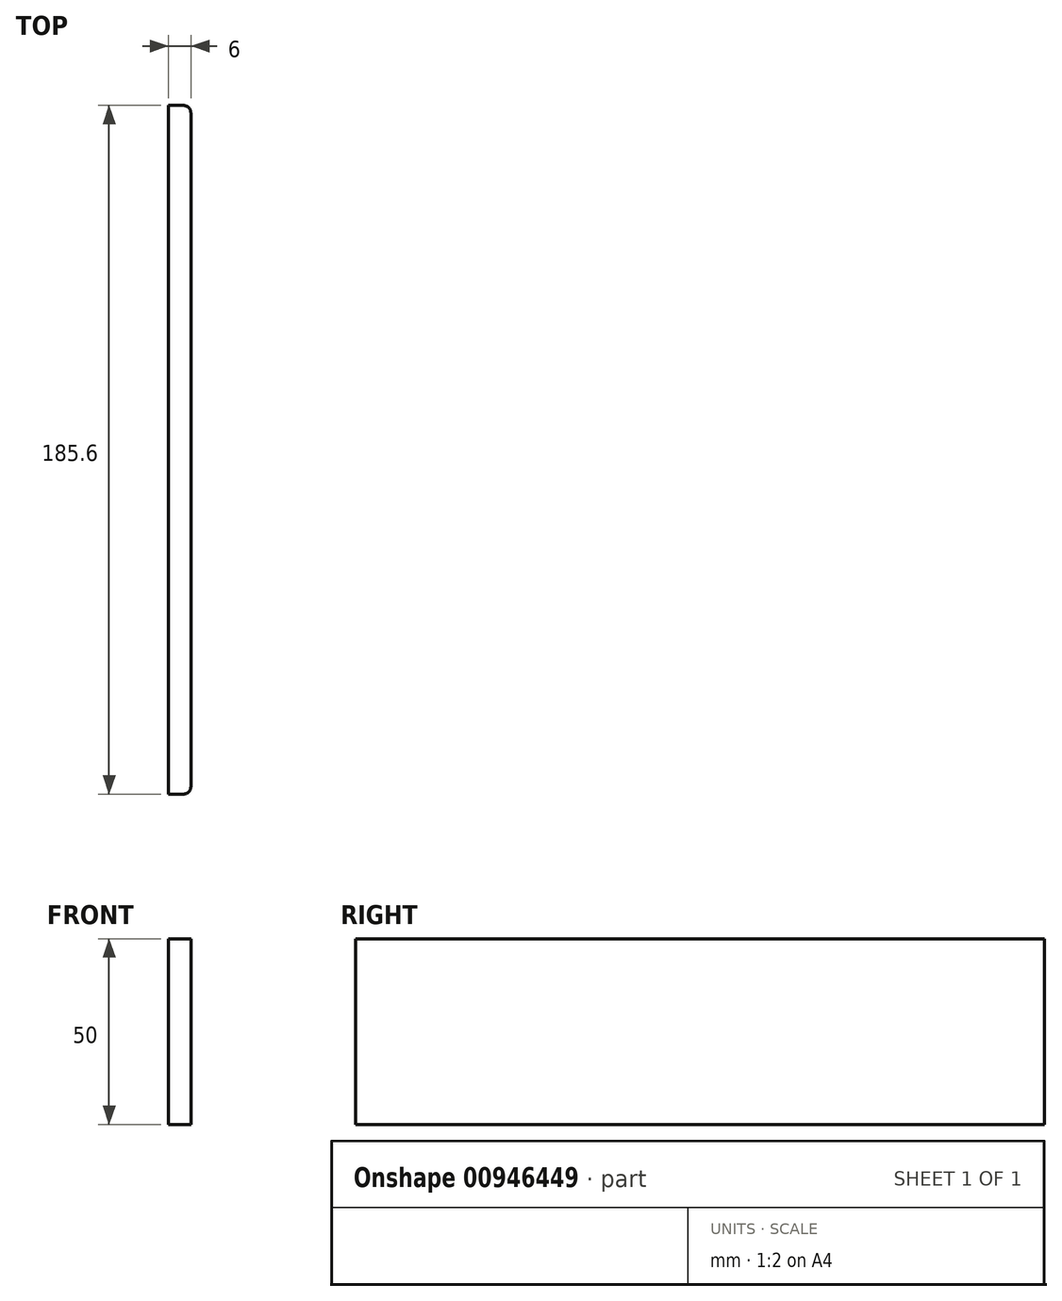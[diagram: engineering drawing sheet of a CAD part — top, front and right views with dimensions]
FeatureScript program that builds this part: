
annotation { "Feature Type Name" : "Feature", "Feature Type Description" : "" }
export const myFeature = defineFeature(function(context is Context, id is Id, definition is map)
    precondition{}
    {
        {
            var Q0;
            Q0=qCreatedBy(makeId("Right.planeOp"),FACE);
            var sketch = newSketch(context, id + "F0", { "sketchPlane" : qUnion([Q0])});
            skLineSegment(sketch, "E0.bottom", {"start": v(92.8, 25) * mm, "end": v(-92.8, 25) * mm});
            skLineSegment(sketch, "E0.top", {"start": v(92.8, -25) * mm, "end": v(-92.8, -25) * mm});
            skLineSegment(sketch, "E0.left", {"start": v(92.8, 25) * mm, "end": v(92.8, -25) * mm});
            skLineSegment(sketch, "E0.right", {"start": v(-92.8, 25) * mm, "end": v(-92.8, -25) * mm});
            skPoint(sketch, "E0.middle", {"position": v(0, 0) * mm});
            skSolve(sketch);
        }
        {
            var Q0;
            Q0=makeQuery(id+"F0.imprint","IMPRINT",FACE,{"disambiguationData":[TD([[makeQuery(id+"F0.imprint","IMPRINT",EDGE,{"derivedFrom":sQuery(id+"F0.wireOp",EDGE,"E0.bottom")}),1.0]])]});
            extrude(context, id + "F1", {"entities" : qUnion([Q0]), "depth" : 6 * mm, "offsetDistance" : 25 * mm});
        }
        {
            var Q0;
            Q0=makeQuery(id+"F1.opExtrude","CAP_EDGE",EDGE,{"disambiguationData":[OSD([sQuery(id+"F0.wireOp",EDGE,"E0.right")])],"isStart":false});
            var Q1;
            Q1=makeQuery(id+"F1.opExtrude","CAP_EDGE",EDGE,{"disambiguationData":[OSD([sQuery(id+"F0.wireOp",EDGE,"E0.left")])],"isStart":false});
            fillet(context, id + "F2", {"entities" : qUnion([Q0, Q1]), "radius" : 2 * mm, "tangentPropagation" : true, "allowEdgeOverflow" : false});
        }
    });
